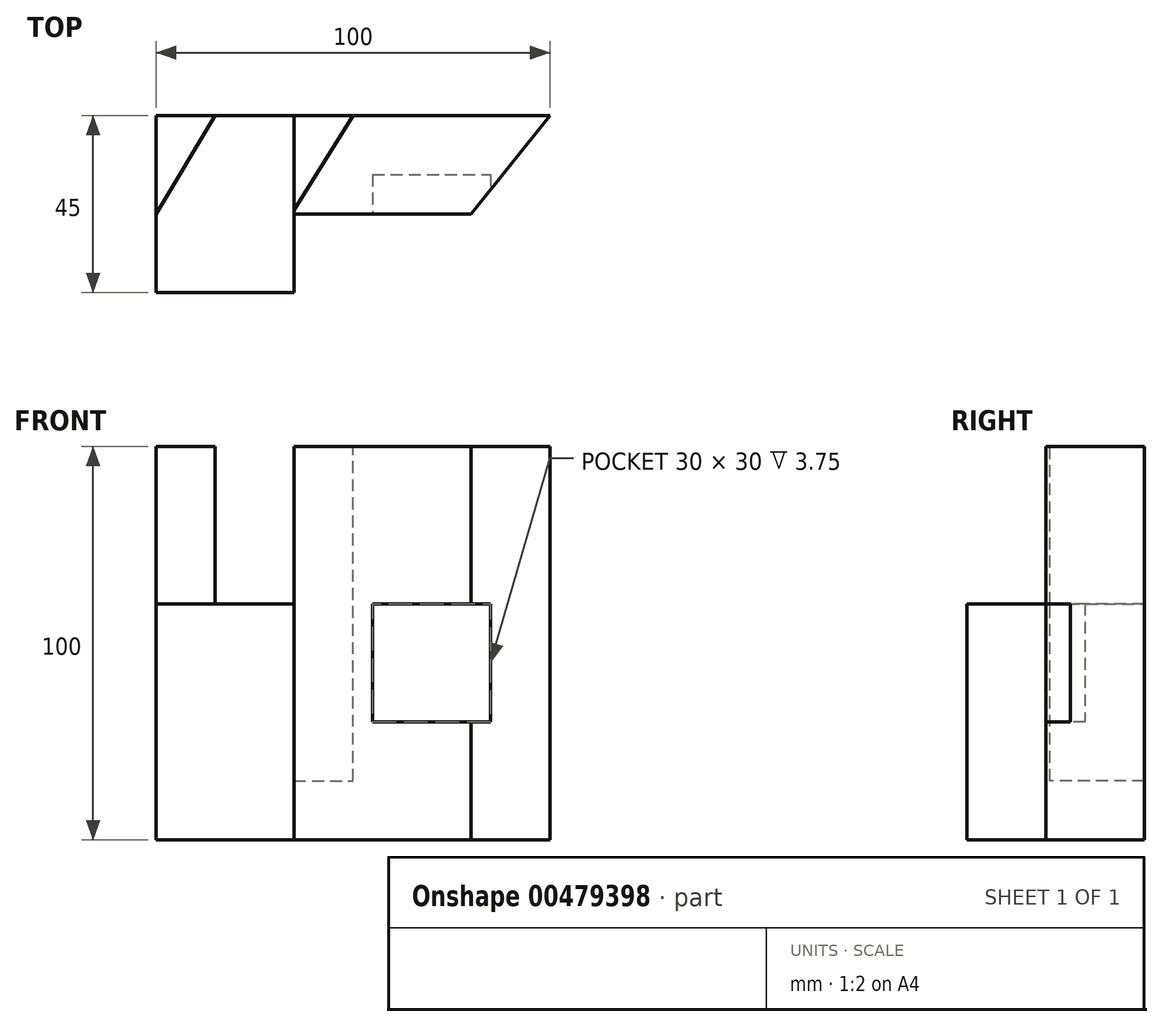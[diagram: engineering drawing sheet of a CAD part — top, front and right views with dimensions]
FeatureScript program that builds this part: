
annotation { "Feature Type Name" : "Feature", "Feature Type Description" : "" }
export const myFeature = defineFeature(function(context is Context, id is Id, definition is map)
    precondition{}
    {
        {
            var Q0;
            Q0=qCreatedBy(makeId("Top.planeOp"),FACE);
            var sketch = newSketch(context, id + "F0", { "sketchPlane" : qUnion([Q0])});
            skLineSegment(sketch, "E0.bottom", {"start": v(0, 0) * mm, "end": v(100, 0) * mm});
            skLineSegment(sketch, "E0.top", {"start": v(0, 45) * mm, "end": v(100, 45) * mm});
            skLineSegment(sketch, "E0.left", {"start": v(0, 0) * mm, "end": v(0, 45) * mm});
            skLineSegment(sketch, "E0.right", {"start": v(100, 0) * mm, "end": v(100, 45) * mm});
            skSolve(sketch);
        }
        {
            var Q0;
            Q0 = qSketchRegion(id + "F0", true);
            extrude(context, id + "F1", {"entities" : qUnion([Q0]), "depth" : 100 * mm});
        }
        {
            var Q0;
            Q0=makeQuery(id+"F1.opExtrude","CAP_FACE",FACE,{"disambiguationData":[OSD([sQuery(id+"F0.wireOp",EDGE,"E0.bottom"),sQuery(id+"F0.wireOp",EDGE,"E0.top"),sQuery(id+"F0.wireOp",EDGE,"E0.left"),sQuery(id+"F0.wireOp",EDGE,"E0.right")])],"isStart":false});
            var sketch = newSketch(context, id + "F2", { "sketchPlane" : qUnion([Q0])});
            skLineSegment(sketch, "E1.bottom", {"start": v(0, 45) * mm, "end": v(15, 45) * mm});
            skLineSegment(sketch, "E1.left", {"start": v(0, 45) * mm, "end": v(0, 20) * mm});
            skLineSegment(sketch, "E2", {"start": v(15, 45) * mm, "end": v(0, 20) * mm});
            skLineSegment(sketch, "E3.bottom", {"start": v(0, 0) * mm, "end": v(35, 0) * mm});
            skLineSegment(sketch, "E3.top", {"start": v(0, 45) * mm, "end": v(35, 45) * mm});
            skLineSegment(sketch, "E3.left", {"start": v(0, 0) * mm, "end": v(0, 45) * mm});
            skLineSegment(sketch, "E3.right", {"start": v(35, 0) * mm, "end": v(35, 45) * mm});
            skSolve(sketch);
        }
        {
            var Q0;
            {var subQ2=sQuery(id+"F2.wireOp",EDGE,"E2");Q0=makeQuery(id+"F2.imprint","IMPRINT",FACE,{"disambiguationData":[TD([[makeQuery(id+"F2.imprint","IMPRINT",EDGE,{"derivedFrom":subQ2}),1.0]])]});}
            extrude(context, id + "F3", {"entities" : qUnion([Q0]), "operationType" : NewBodyOperationType.REMOVE, "oppositeDirection" : true, "depth" : 40 * mm});
        }
        {
            var Q0;
            {var subQ0=sQuery(id+"F0.wireOp",EDGE,"E0.bottom");var subQ1=sQuery(id+"F0.wireOp",EDGE,"E0.right");var subQ2=sQuery(id+"F0.wireOp",EDGE,"E0.top");Q0=makeQuery(id+"F3.boolean.opBoolean","SPLIT",FACE,{"disambiguationData":[TD([makeQuery(id+"F1.opExtrude","SWEPT_FACE",FACE,{"disambiguationData":[OSD([subQ0])]})])],"derivedFrom":makeQuery(id+"F1.opExtrude","CAP_FACE",FACE,{"disambiguationData":[OSD([subQ0,subQ2,sQuery(id+"F0.wireOp",EDGE,"E0.left"),subQ1])],"isStart":false})});}
            var sketch = newSketch(context, id + "F4", { "sketchPlane" : qUnion([Q0])});
            skLineSegment(sketch, "E4.bottom", {"start": v(35, 0) * mm, "end": v(80, 0) * mm});
            skLineSegment(sketch, "E4.top", {"start": v(35, 20) * mm, "end": v(80, 20) * mm});
            skLineSegment(sketch, "E4.left", {"start": v(35, 0) * mm, "end": v(35, 20) * mm});
            skLineSegment(sketch, "E4.right", {"start": v(80, 0) * mm, "end": v(80, 20) * mm});
            skSolve(sketch);
        }
        {
            var Q0;
            Q0=makeQuery(id+"F4.imprint","IMPRINT",FACE,{"disambiguationData":[TD([[makeQuery(id+"F4.imprint","IMPRINT",EDGE,{"derivedFrom":sQuery(id+"F4.wireOp",EDGE,"E4.bottom")}),1.0]])]});
            extrude(context, id + "F5", {"entities" : qUnion([Q0]), "operationType" : NewBodyOperationType.REMOVE, "endBound" : BoundingType.THROUGH_ALL, "oppositeDirection" : true, "depth" : 25 * mm});
        }
        {
            var Q0;
            {var subQ0=sQuery(id+"F0.wireOp",EDGE,"E0.bottom");var subQ1=sQuery(id+"F0.wireOp",EDGE,"E0.right");var subQ2=sQuery(id+"F0.wireOp",EDGE,"E0.top");Q0=makeQuery(id+"F3.boolean.opBoolean","SPLIT",FACE,{"disambiguationData":[TD([makeQuery(id+"F1.opExtrude","SWEPT_FACE",FACE,{"disambiguationData":[OSD([subQ0])]})])],"derivedFrom":makeQuery(id+"F1.opExtrude","CAP_FACE",FACE,{"disambiguationData":[OSD([subQ0,subQ2,sQuery(id+"F0.wireOp",EDGE,"E0.left"),subQ1])],"isStart":false})});}
            var sketch = newSketch(context, id + "F6", { "sketchPlane" : qUnion([Q0])});
            skLineSegment(sketch, "E5", {"start": v(80, 20) * mm, "end": v(100, 45) * mm});
            skSolve(sketch);
        }
        {
            var Q0;
            Q0 = qSketchRegion(id + "F6", true);
            var Q1;
            Q1=makeQuery(id+"F6.imprint","IMPRINT",FACE,{"disambiguationData":[TD([[makeQuery(id+"F6.imprint","IMPRINT",EDGE,{"derivedFrom":sQuery(id+"F6.wireOp",EDGE,"E5")}),-1.0]])]});
            extrude(context, id + "F7", {"entities" : qUnion([Q0, Q1]), "operationType" : NewBodyOperationType.REMOVE, "endBound" : BoundingType.THROUGH_ALL, "oppositeDirection" : true, "depth" : 25 * mm});
        }
        {
            var Q0;
            {var subQ0=sQuery(id+"F0.wireOp",EDGE,"E0.bottom");var subQ1=sQuery(id+"F0.wireOp",EDGE,"E0.right");var subQ2=sQuery(id+"F0.wireOp",EDGE,"E0.top");Q0=makeQuery(id+"F3.boolean.opBoolean","SPLIT",FACE,{"disambiguationData":[TD([makeQuery(id+"F1.opExtrude","SWEPT_FACE",FACE,{"disambiguationData":[OSD([subQ0])]})])],"derivedFrom":makeQuery(id+"F1.opExtrude","CAP_FACE",FACE,{"disambiguationData":[OSD([subQ0,subQ2,sQuery(id+"F0.wireOp",EDGE,"E0.left"),subQ1])],"isStart":false})});}
            var sketch = newSketch(context, id + "F8", { "sketchPlane" : qUnion([Q0])});
            skLineSegment(sketch, "E6", {"start": v(35, 45) * mm, "end": v(50, 45) * mm});
            skLineSegment(sketch, "E7", {"start": v(35, 45) * mm, "end": v(35, 21) * mm});
            skLineSegment(sketch, "E8", {"start": v(50, 45) * mm, "end": v(35, 21) * mm});
            skSolve(sketch);
        }
        {
            var Q0;
            Q0 = qSketchRegion(id + "F8", true);
            extrude(context, id + "F9", {"entities" : qUnion([Q0]), "operationType" : NewBodyOperationType.REMOVE, "oppositeDirection" : true, "depth" : 85 * mm});
        }
        {
            var Q0;
            Q0=makeQuery(id+"F5.boolean.opBoolean","COPY",FACE,{"derivedFrom":makeQuery(id+"F5.opExtrude","SWEPT_FACE",FACE,{"disambiguationData":[OSD([sQuery(id+"F4.wireOp",EDGE,"E4.top")])]})});
            var sketch = newSketch(context, id + "F10", { "sketchPlane" : qUnion([Q0])});
            skLineSegment(sketch, "E9.bottom", {"start": v(55, 60) * mm, "end": v(85, 60) * mm});
            skLineSegment(sketch, "E9.top", {"start": v(55, 30) * mm, "end": v(85, 30) * mm});
            skLineSegment(sketch, "E9.left", {"start": v(55, 60) * mm, "end": v(55, 30) * mm});
            skLineSegment(sketch, "E9.right", {"start": v(85, 60) * mm, "end": v(85, 30) * mm});
            skSolve(sketch);
        }
        {
            var Q0;
            Q0 = qSketchRegion(id + "F10", true);
            extrude(context, id + "F11", {"entities" : qUnion([Q0]), "operationType" : NewBodyOperationType.REMOVE, "oppositeDirection" : true, "depth" : 10 * mm});
        }
    });
